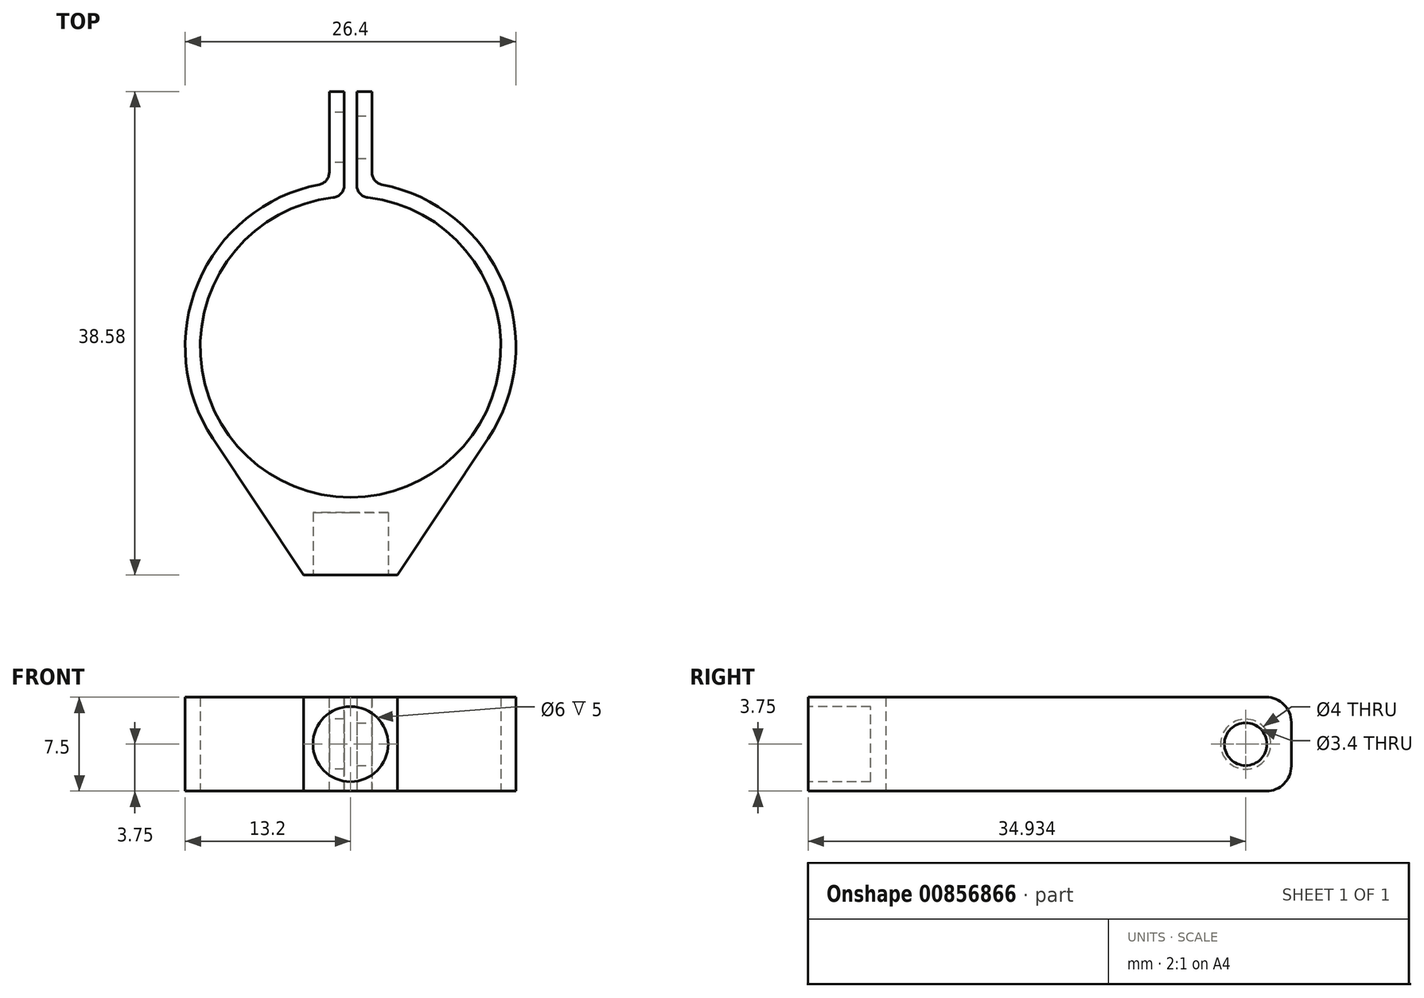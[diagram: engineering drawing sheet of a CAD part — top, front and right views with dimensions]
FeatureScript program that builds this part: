
annotation { "Feature Type Name" : "Feature", "Feature Type Description" : "" }
export const myFeature = defineFeature(function(context is Context, id is Id, definition is map)
    precondition{}
    {
        {
            var Q0;
            Q0=qCreatedBy(makeId("Top.planeOp"),FACE);
            var sketch = newSketch(context, id + "F0", { "sketchPlane" : qUnion([Q0])});
            skCircle(sketch, "E0", {"center": v(0, 0) * mm, "radius": 12 * mm});
            skCircle(sketch, "E1.0", {"center": v(0, 0) * mm, "radius": 13.2 * mm});
            skLineSegment(sketch, "E2", {"start": v(-0.5, 11.99) * mm, "end": v(-0.5, 20.38) * mm});
            skLineSegment(sketch, "E3", {"start": v(-0.5, 20.38) * mm, "end": v(-1.7, 20.38) * mm});
            skLineSegment(sketch, "E4", {"start": v(-1.7, 20.38) * mm, "end": v(-1.7, 11.88) * mm});
            skLineSegment(sketch, "E5.MirrorCS", {"start": v(0.5, 11.99) * mm, "end": v(0.5, 20.38) * mm});
            skLineSegment(sketch, "E6.MirrorCS", {"start": v(0.5, 20.38) * mm, "end": v(1.7, 20.38) * mm});
            skLineSegment(sketch, "E7.MirrorCS", {"start": v(1.7, 20.38) * mm, "end": v(1.7, 11.88) * mm});
            skLineSegment(sketch, "E8", {"start": v(-11, -7.3) * mm, "end": v(-3.75, -18.2) * mm});
            skLineSegment(sketch, "E9", {"start": v(-3.75, -18.2) * mm, "end": v(3.75, -18.2) * mm});
            skLineSegment(sketch, "E10", {"start": v(3.75, -18.2) * mm, "end": v(11, -7.3) * mm});
            skPoint(sketch, "E11", {"position": v(0, -18.2) * mm});
            skPoint(sketch, "E12", {"position": v(0, -13.2) * mm});
            skSolve(sketch);
        }
        {
            var Q0;
            {var subQ0=sQuery(id+"F0.wireOp",EDGE,"E8");Q0=makeQuery(id+"F0.imprint","IMPRINT",FACE,{"disambiguationData":[TD([[makeQuery(id+"F0.imprint","IMPRINT",EDGE,{"derivedFrom":subQ0}),1.0]])]});}
            var Q1;
            {var subQ5=sQuery(id+"F0.wireOp",EDGE,"E4");var subQ7=sQuery(id+"F0.wireOp",EDGE,"E0");var subQ9=makeQuery(id+"F0.imprint","INTERSECT",VERTEX,{"derivedFrom":[subQ7,subQ5]});Q1=makeQuery(id+"F0.imprint","IMPRINT",FACE,{"disambiguationData":[TD([[makeQuery(id+"F0.imprint","IMPRINT",EDGE,{"disambiguationData":[TD([[subQ9,-1.0]])],"derivedFrom":subQ7}),-1.0]])]});}
            var Q2;
            {var subQ5=sQuery(id+"F0.wireOp",EDGE,"E6.MirrorCS");Q2=makeQuery(id+"F0.imprint","IMPRINT",FACE,{"disambiguationData":[TD([[makeQuery(id+"F0.imprint","IMPRINT",EDGE,{"derivedFrom":subQ5}),-1.0]])]});}
            var Q3;
            {var subQ5=sQuery(id+"F0.wireOp",EDGE,"E3");Q3=makeQuery(id+"F0.imprint","IMPRINT",FACE,{"disambiguationData":[TD([[makeQuery(id+"F0.imprint","IMPRINT",EDGE,{"derivedFrom":subQ5}),1.0]])]});}
            var Q4;
            {var subQ0=sQuery(id+"F0.wireOp",EDGE,"E2");var subQ1=sQuery(id+"F0.wireOp",EDGE,"E0");var subQ2=makeQuery(id+"F0.imprint","INTERSECT",VERTEX,{"derivedFrom":[subQ1,subQ0]});Q4=makeQuery(id+"F0.imprint","IMPRINT",FACE,{"disambiguationData":[TD([[makeQuery(id+"F0.imprint","IMPRINT",EDGE,{"disambiguationData":[TD([[subQ2,-1.0]])],"derivedFrom":subQ1}),-1.0]])]});}
            var Q5;
            {var subQ0=sQuery(id+"F0.wireOp",EDGE,"E5.MirrorCS");var subQ1=sQuery(id+"F0.wireOp",EDGE,"E0");var subQ2=makeQuery(id+"F0.imprint","INTERSECT",VERTEX,{"derivedFrom":[subQ1,subQ0]});Q5=makeQuery(id+"F0.imprint","IMPRINT",FACE,{"disambiguationData":[TD([[makeQuery(id+"F0.imprint","IMPRINT",EDGE,{"disambiguationData":[TD([[subQ2,1.0]])],"derivedFrom":subQ1}),-1.0]])]});}
            extrude(context, id + "F1", {"entities" : qUnion([Q0, Q1, Q2, Q3, Q4, Q5]), "depth" : 7.5 * mm, "offsetDistance" : 25 * mm});
        }
        {
            var Q0;
            Q0=makeQuery(id+"F1.opExtrude","SWEPT_FACE",FACE,{"disambiguationData":[OSD([sQuery(id+"F0.wireOp",EDGE,"E9")])]});
            var sketch = newSketch(context, id + "F2", { "sketchPlane" : qUnion([Q0])});
            skCircle(sketch, "E13", {"center": v(0, 3.75) * mm, "radius": 3 * mm});
            skLineSegment(sketch, "E14", {"start": v(0, 7.5) * mm, "end": v(0, 0) * mm, "construction": true});
            skSolve(sketch);
        }
        {
            var Q0;
            Q0=makeQuery(id+"F2.imprint","IMPRINT",FACE,{"disambiguationData":[TD([[makeQuery(id+"F2.imprint","IMPRINT",EDGE,{"derivedFrom":sQuery(id+"F2.wireOp",EDGE,"E13")}),1.0]])]});
            extrude(context, id + "F3", {"entities" : qUnion([Q0]), "operationType" : NewBodyOperationType.REMOVE, "oppositeDirection" : true, "depth" : 5 * mm, "offsetDistance" : 25 * mm});
        }
        {
            var Q0;
            Q0=makeQuery(id+"F1.opExtrude","SWEPT_FACE",FACE,{"disambiguationData":[OSD([sQuery(id+"F0.wireOp",EDGE,"E4")])]});
            var sketch = newSketch(context, id + "F4", { "sketchPlane" : qUnion([Q0])});
            skCircle(sketch, "E15", {"center": v(-16.73, 3.75) * mm, "radius": 2 * mm});
            skLineSegment(sketch, "E16", {"start": v(-16.73, 7.5) * mm, "end": v(-16.73, 0) * mm, "construction": true});
            skSolve(sketch);
        }
        {
            var Q0;
            Q0=makeQuery(id+"F4.imprint","IMPRINT",FACE,{"disambiguationData":[TD([[makeQuery(id+"F4.imprint","IMPRINT",EDGE,{"derivedFrom":sQuery(id+"F4.wireOp",EDGE,"E15")}),1.0]])]});
            var Q1;
            Q1=makeQuery(id+"F1.opExtrude","SWEPT_FACE",FACE,{"disambiguationData":[OSD([sQuery(id+"F0.wireOp",EDGE,"E2")])]});
            extrude(context, id + "F5", {"entities" : qUnion([Q0]), "operationType" : NewBodyOperationType.REMOVE, "endBound" : BoundingType.UP_TO_SURFACE, "oppositeDirection" : true, "depth" : 25 * mm, "endBoundEntityFace" : qUnion([Q1]), "offsetDistance" : 25 * mm});
        }
        {
            var Q0;
            Q0=makeQuery(id+"F1.opExtrude","SWEPT_FACE",FACE,{"disambiguationData":[OSD([sQuery(id+"F0.wireOp",EDGE,"E7.MirrorCS")])]});
            var sketch = newSketch(context, id + "F6", { "sketchPlane" : qUnion([Q0])});
            skLineSegment(sketch, "E17", {"start": v(16.73, 7.5) * mm, "end": v(16.73, 0) * mm, "construction": true});
            skCircle(sketch, "E18", {"center": v(16.73, 3.75) * mm, "radius": 1.7 * mm});
            skSolve(sketch);
        }
        {
            var Q0;
            Q0=makeQuery(id+"F6.imprint","IMPRINT",FACE,{"disambiguationData":[TD([[makeQuery(id+"F6.imprint","IMPRINT",EDGE,{"derivedFrom":sQuery(id+"F6.wireOp",EDGE,"E18")}),1.0]])]});
            var Q1;
            Q1=makeQuery(id+"F1.opExtrude","SWEPT_FACE",FACE,{"disambiguationData":[OSD([sQuery(id+"F0.wireOp",EDGE,"E5.MirrorCS")])]});
            extrude(context, id + "F7", {"entities" : qUnion([Q0]), "operationType" : NewBodyOperationType.REMOVE, "endBound" : BoundingType.UP_TO_SURFACE, "oppositeDirection" : true, "depth" : 25 * mm, "endBoundEntityFace" : qUnion([Q1]), "offsetDistance" : 25 * mm});
        }
        {
            var Q0;
            Q0=makeQuery(id+"F3.boolean.opBoolean","COPY",EDGE,{"derivedFrom":makeQuery(id+"F3.opExtrude","CAP_EDGE",EDGE,{"disambiguationData":[OSD([sQuery(id+"F2.wireOp",EDGE,"E13")])],"isStart":true})});
            var Q1;
            Q1=makeQuery(id+"F1.opExtrude","SWEPT_EDGE",EDGE,{"disambiguationData":[OSD([sQuery(id+"F0.wireOp",EDGE,"E0"),sQuery(id+"F0.wireOp",EDGE,"E2")])]});
            var Q2;
            Q2=makeQuery(id+"F1.opExtrude","SWEPT_EDGE",EDGE,{"disambiguationData":[OSD([sQuery(id+"F0.wireOp",EDGE,"E0"),sQuery(id+"F0.wireOp",EDGE,"E5.MirrorCS")])]});
            var Q3;
            Q3=makeQuery(id+"F1.opExtrude","SWEPT_EDGE",EDGE,{"disambiguationData":[OSD([sQuery(id+"F0.wireOp",EDGE,"E1.0"),sQuery(id+"F0.wireOp",EDGE,"E4")])]});
            var Q4;
            Q4=makeQuery(id+"F1.opExtrude","SWEPT_EDGE",EDGE,{"disambiguationData":[OSD([sQuery(id+"F0.wireOp",EDGE,"E1.0"),sQuery(id+"F0.wireOp",EDGE,"E7.MirrorCS")])]});
            fillet(context, id + "F8", {"entities" : qUnion([Q0, Q1, Q2, Q3, Q4]), "radius" : 1 * mm, "tangentPropagation" : true, "allowEdgeOverflow" : false});
        }
        {
            var Q0;
            Q0=makeQuery(id+"F1.opExtrude","CAP_EDGE",EDGE,{"disambiguationData":[OSD([sQuery(id+"F0.wireOp",EDGE,"E3")])],"isStart":false});
            var Q1;
            Q1=makeQuery(id+"F1.opExtrude","CAP_EDGE",EDGE,{"disambiguationData":[OSD([sQuery(id+"F0.wireOp",EDGE,"E6.MirrorCS")])],"isStart":false});
            var Q2;
            Q2=makeQuery(id+"F1.opExtrude","CAP_EDGE",EDGE,{"disambiguationData":[OSD([sQuery(id+"F0.wireOp",EDGE,"E6.MirrorCS")])],"isStart":true});
            var Q3;
            Q3=makeQuery(id+"F1.opExtrude","CAP_EDGE",EDGE,{"disambiguationData":[OSD([sQuery(id+"F0.wireOp",EDGE,"E3")])],"isStart":true});
            fillet(context, id + "F9", {"entities" : qUnion([Q0, Q1, Q2, Q3]), "radius" : 2 * mm, "tangentPropagation" : true, "allowEdgeOverflow" : false});
        }
    });
